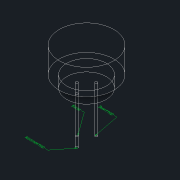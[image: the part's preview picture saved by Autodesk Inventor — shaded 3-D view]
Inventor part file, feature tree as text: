
AUTODESK INVENTOR PART (.ipt)
format: ipt  version: 2021.2 (Build 252289000, 289)  size: 116,736 bytes
history: native  units: mm
features: other x8, extrude x5, sketch x3
ambient origin geometry x8: Origin, YZ Plane, XZ Plane, XY Plane, X Axis, Y Axis, Z Axis, Center Point
bodies: Body1 (feature_tree), Body2 (feature_tree), Body3 (feature_tree), Body4 (feature_tree)
feature tree (16):
  other  "Твердое тело1"
  other  "Аннотации"
  extrude  "Выдавливание1"  Depth=5.5mm TaperAngle=0.0deg
  extrude  "Выдавливание2"  Depth=11.7mm
  sketch  "Эскиз3"
  extrude  "Выдавливание3"  Depth=2.5mm TaperAngle=0.0deg
  extrude  "Выдавливание4"  Depth=8.5mm
  extrude  "Выдавливание5"  Depth=4.2mm
  sketch  "Эскиз1"
  sketch  "Эскиз2"
  other  "Твердое тело2"
  other  "Твердое тело3"
  other  "Твердое тело4"
  other  "Текст на выноске 1"
  other  "Текст на выноске 2"
  other  "Текст на выноске 3"
